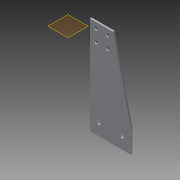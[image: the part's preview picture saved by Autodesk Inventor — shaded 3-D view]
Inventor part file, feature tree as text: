
AUTODESK INVENTOR PART (.ipt)
format: ipt  version: 2014 SP1 (Build 180222100, 222)  size: 168,448 bytes
history: native  units: in
note: dims shown in document units (in); Inventor stores cm internally (conversion verified against a paired STEP export)
features: other x4, sheet_metal_op x1, plane x1, fillet x1, sketch x1
ambient origin geometry x8: Origin, YZ Plane, XZ Plane, XY Plane, X Axis, Y Axis, Z Axis, Center Point
bodies: Solid1 (feature_tree)
feature tree (8):
  sheet_metal_op  "Face1"
  plane  "Work Plane1"
  fillet  "Fillet5"  Radius=0.163in
  sketch  "Sketch1"  dims[d4=0.7874in d6=1.0in d7=0.3937in d9=1.0in d11=0.0625in d22=0.5in d28=0.187in d29=0.25in d34=0.75in d47=0.125in d48=0.25in d49=0.25in d50=0.375in d51=0.0625in d52=0.0in d54=1.0in d55=4.1875in d56=1.0in d57=1.75in d58=0.375in d80=0.5in d81=0.25in d82=0.25in d83=0.7874in d85=0.5in d86=0.7874in d88=0.5in d0=0.125in d1=0.125in d3=0.0in]
  other  "Plate1"
  other  "Cut3"
  other  "Definition1"
  other  "Cut1"
